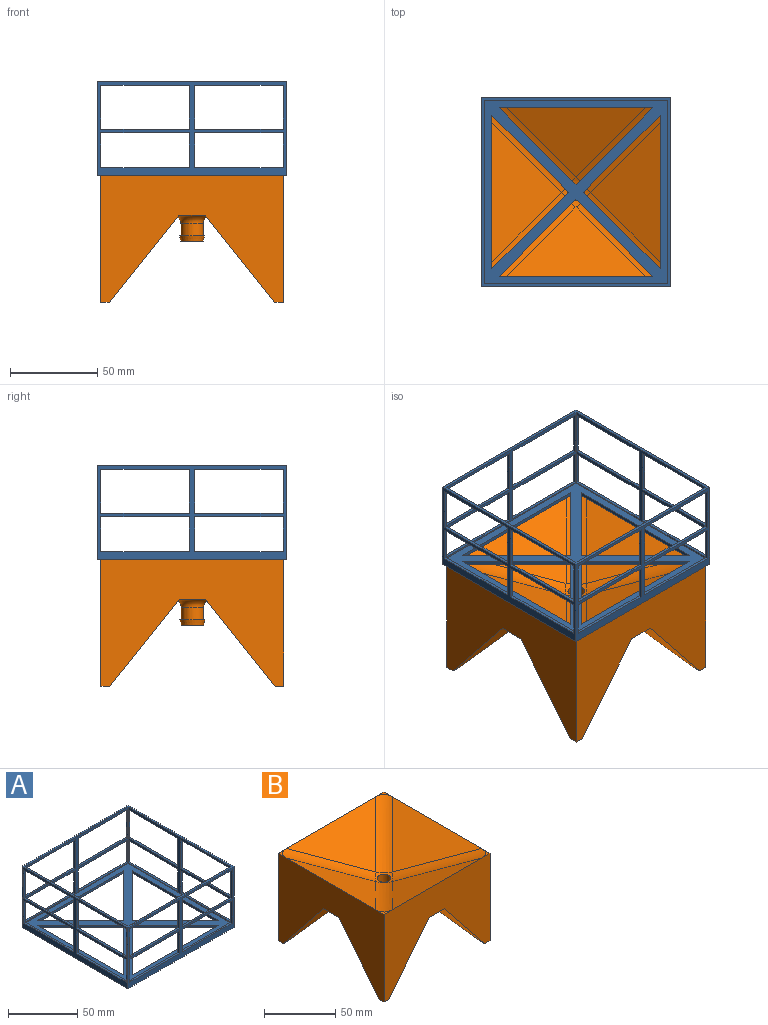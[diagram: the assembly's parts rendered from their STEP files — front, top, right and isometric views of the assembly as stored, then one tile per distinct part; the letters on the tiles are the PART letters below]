
ASSEMBLY  parts=2 mates=1
PART A: 92 faces, bbox 108.6x108.6x54 mm
  f0: plane 105.4x105.4mm, normal (0,0,1), area 3345mm2, adj f2,f3,f4,f5,f6,f7,f8,f9
  f1: plane 108.6x54mm, normal (-1,0,0), area 1272.1mm2, adj f12,f16,f19,f24,f25,f26,f27,f28
  f2: plane 105.4x50mm, normal (1,0,0), area 677.7mm2, adj f0,f19,f25,f26,f27,f28,f29,f30
  f3: plane 44.06x44.06mm, normal (0.71,0.71,0), area 124.6mm2, adj f0,f4,f17,f18
  f4: plane 44.06x44.06mm, normal (0.71,-0.71,0), area 124.6mm2, adj f0,f3,f17,f18
  f5: plane 44.06x44.06mm, normal (0.71,0.71,0), area 124.6mm2, adj f0,f6,f13,f18
  f6: plane 88.11x2mm, normal (0,-1,0), area 176.2mm2, adj f0,f5,f13,f18
  f7: plane 44.06x44.06mm, normal (0.71,-0.71,0), area 124.6mm2, adj f0,f8,f14,f18
  f8: plane 44.06x44.06mm, normal (-0.71,-0.71,0), area 124.6mm2, adj f0,f7,f14,f18
  f9: plane 88.11x2mm, normal (1,0,0), area 176.2mm2, adj f0,f10,f15,f18
  f10: plane 44.06x44.06mm, normal (-0.71,-0.71,0), area 124.6mm2, adj f0,f9,f15,f18
  f11: plane 108.6x54mm, normal (1,0,0), area 1272.1mm2, adj f12,f16,f19,f24,f59,f60,f61,f62
  f12: plane 108.6x54mm, normal (0,1,0), area 1272.1mm2, adj f1,f11,f19,f24,f76,f77,f78,f79
  f13: plane 44.06x44.06mm, normal (-0.71,0.71,0), area 124.6mm2, adj f0,f5,f6,f18
  f14: plane 88.11x2mm, normal (0,1,0), area 176.2mm2, adj f0,f7,f8,f18
  f15: plane 44.06x44.06mm, normal (-0.71,0.71,0), area 124.6mm2, adj f0,f9,f10,f18
  f16: plane 108.6x54mm, normal (0,-1,0), area 1272.1mm2, adj f1,f11,f19,f24,f42,f43,f44,f45
  f17: plane 88.11x2mm, normal (-1,0,0), area 176.2mm2, adj f0,f3,f4,f18
  f18: plane 105.4x105.4mm, normal (0,0,-1), area 3345mm2, adj f3,f4,f5,f6,f7,f8,f9,f10
  f19: plane 108.6x108.6mm, normal (0,0,1), area 684.8mm2, adj f1,f2,f11,f12,f16,f41,f58,f75
  f20: plane 105.4x2mm, normal (0,1,0), area 210.8mm2, adj f18,f21,f23,f24
  f21: plane 105.4x2mm, normal (-1,0,0), area 210.8mm2, adj f18,f20,f22,f24
  f22: plane 105.4x2mm, normal (0,-1,0), area 210.8mm2, adj f18,f21,f23,f24
  f23: plane 105.4x2mm, normal (1,0,0), area 210.8mm2, adj f18,f20,f22,f24
  f24: plane 108.6x108.6mm, normal (0,0,-1), area 684.8mm2, adj f1,f11,f12,f16,f20,f21,f22,f23
  f25: plane 50.8x1.6mm, normal (0,0,-1), area 81.3mm2, adj f1,f2,f26,f28
  f26: plane 25.2x1.6mm, normal (0,-1,0), area 40.3mm2, adj f1,f2,f25,f27
  f27: plane 50.8x1.6mm, normal (0,0,1), area 81.3mm2, adj f1,f2,f26,f28
  f28: plane 25.2x1.6mm, normal (0,1,0), area 40.3mm2, adj f1,f2,f25,f27
  f29: plane 50.8x1.6mm, normal (0,0,-1), area 81.3mm2, adj f1,f2,f30,f32
  f30: plane 20x1.6mm, normal (0,-1,0), area 32mm2, adj f1,f2,f29,f31
  f31: plane 50.8x1.6mm, normal (0,0,1), area 81.3mm2, adj f1,f2,f30,f32
  f32: plane 20x1.6mm, normal (0,1,0), area 32mm2, adj f1,f2,f29,f31
  f33: plane 50.8x1.6mm, normal (0,0,-1), area 81.3mm2, adj f1,f2,f34,f36
  f34: plane 20x1.6mm, normal (0,-1,0), area 32mm2, adj f1,f2,f33,f35
  f35: plane 50.8x1.6mm, normal (0,0,1), area 81.3mm2, adj f1,f2,f34,f36
  f36: plane 20x1.6mm, normal (0,1,0), area 32mm2, adj f1,f2,f33,f35
  f37: plane 50.8x1.6mm, normal (0,0,-1), area 81.3mm2, adj f1,f2,f38,f40
  f38: plane 25.2x1.6mm, normal (0,-1,0), area 40.3mm2, adj f1,f2,f37,f39
  f39: plane 50.8x1.6mm, normal (0,0,1), area 81.3mm2, adj f1,f2,f38,f40
  f40: plane 25.2x1.6mm, normal (0,1,0), area 40.3mm2, adj f1,f2,f37,f39
  f41: plane 105.4x50mm, normal (0,1,0), area 677.7mm2, adj f0,f2,f19,f42,f43,f44,f45,f46
  f42: plane 50.8x1.6mm, normal (0,0,-1), area 81.3mm2, adj f16,f41,f43,f45
  f43: plane 25.2x1.6mm, normal (1,0,0), area 40.3mm2, adj f16,f41,f42,f44
  f44: plane 50.8x1.6mm, normal (0,0,1), area 81.3mm2, adj f16,f41,f43,f45
  f45: plane 25.2x1.6mm, normal (-1,0,0), area 40.3mm2, adj f16,f41,f42,f44
  f46: plane 50.8x1.6mm, normal (0,0,-1), area 81.3mm2, adj f16,f41,f47,f49
  f47: plane 20x1.6mm, normal (1,0,0), area 32mm2, adj f16,f41,f46,f48
  f48: plane 50.8x1.6mm, normal (0,0,1), area 81.3mm2, adj f16,f41,f47,f49
  f49: plane 20x1.6mm, normal (-1,0,0), area 32mm2, adj f16,f41,f46,f48
  f50: plane 50.8x1.6mm, normal (0,0,-1), area 81.3mm2, adj f16,f41,f51,f53
  f51: plane 20x1.6mm, normal (1,0,0), area 32mm2, adj f16,f41,f50,f52
  f52: plane 50.8x1.6mm, normal (0,0,1), area 81.3mm2, adj f16,f41,f51,f53
  f53: plane 20x1.6mm, normal (-1,0,0), area 32mm2, adj f16,f41,f50,f52
  f54: plane 50.8x1.6mm, normal (0,0,-1), area 81.3mm2, adj f16,f41,f55,f57
  f55: plane 25.2x1.6mm, normal (1,0,0), area 40.3mm2, adj f16,f41,f54,f56
  f56: plane 50.8x1.6mm, normal (0,0,1), area 81.3mm2, adj f16,f41,f55,f57
  f57: plane 25.2x1.6mm, normal (-1,0,0), area 40.3mm2, adj f16,f41,f54,f56
  f58: plane 105.4x50mm, normal (-1,0,0), area 677.7mm2, adj f0,f19,f41,f59,f60,f61,f62,f63
  f59: plane 50.8x1.6mm, normal (0,0,-1), area 81.3mm2, adj f11,f58,f60,f62
  f60: plane 25.2x1.6mm, normal (0,1,0), area 40.3mm2, adj f11,f58,f59,f61
  f61: plane 50.8x1.6mm, normal (0,0,1), area 81.3mm2, adj f11,f58,f60,f62
  f62: plane 25.2x1.6mm, normal (0,-1,0), area 40.3mm2, adj f11,f58,f59,f61
  f63: plane 50.8x1.6mm, normal (0,0,-1), area 81.3mm2, adj f11,f58,f64,f66
  f64: plane 20x1.6mm, normal (0,1,0), area 32mm2, adj f11,f58,f63,f65
  f65: plane 50.8x1.6mm, normal (0,0,1), area 81.3mm2, adj f11,f58,f64,f66
  f66: plane 20x1.6mm, normal (0,-1,0), area 32mm2, adj f11,f58,f63,f65
  f67: plane 50.8x1.6mm, normal (0,0,-1), area 81.3mm2, adj f11,f58,f68,f70
  f68: plane 20x1.6mm, normal (0,1,0), area 32mm2, adj f11,f58,f67,f69
  f69: plane 50.8x1.6mm, normal (0,0,1), area 81.3mm2, adj f11,f58,f68,f70
  f70: plane 20x1.6mm, normal (0,-1,0), area 32mm2, adj f11,f58,f67,f69
  f71: plane 50.8x1.6mm, normal (0,0,-1), area 81.3mm2, adj f11,f58,f72,f74
  f72: plane 25.2x1.6mm, normal (0,1,0), area 40.3mm2, adj f11,f58,f71,f73
  f73: plane 50.8x1.6mm, normal (0,0,1), area 81.3mm2, adj f11,f58,f72,f74
  f74: plane 25.2x1.6mm, normal (0,-1,0), area 40.3mm2, adj f11,f58,f71,f73
  f75: plane 105.4x50mm, normal (0,-1,0), area 677.7mm2, adj f0,f2,f19,f58,f76,f77,f78,f79
  f76: plane 50.8x1.6mm, normal (0,0,-1), area 81.3mm2, adj f12,f75,f77,f79
  f77: plane 25.2x1.6mm, normal (-1,0,0), area 40.3mm2, adj f12,f75,f76,f78
  f78: plane 50.8x1.6mm, normal (0,0,1), area 81.3mm2, adj f12,f75,f77,f79
  f79: plane 25.2x1.6mm, normal (1,0,0), area 40.3mm2, adj f12,f75,f76,f78
  f80: plane 50.8x1.6mm, normal (0,0,-1), area 81.3mm2, adj f12,f75,f81,f83
  f81: plane 20x1.6mm, normal (-1,0,0), area 32mm2, adj f12,f75,f80,f82
  f82: plane 50.8x1.6mm, normal (0,0,1), area 81.3mm2, adj f12,f75,f81,f83
  f83: plane 20x1.6mm, normal (1,0,0), area 32mm2, adj f12,f75,f80,f82
  f84: plane 50.8x1.6mm, normal (0,0,-1), area 81.3mm2, adj f12,f75,f85,f87
  f85: plane 20x1.6mm, normal (-1,0,0), area 32mm2, adj f12,f75,f84,f86
  f86: plane 50.8x1.6mm, normal (0,0,1), area 81.3mm2, adj f12,f75,f85,f87
  f87: plane 20x1.6mm, normal (1,0,0), area 32mm2, adj f12,f75,f84,f86
  f88: plane 50.8x1.6mm, normal (0,0,-1), area 81.3mm2, adj f12,f75,f89,f91
  f89: plane 25.2x1.6mm, normal (-1,0,0), area 40.3mm2, adj f12,f75,f88,f90
  f90: plane 50.8x1.6mm, normal (0,0,1), area 81.3mm2, adj f12,f75,f89,f91
  f91: plane 25.2x1.6mm, normal (1,0,0), area 40.3mm2, adj f12,f75,f88,f90
PART B: 39 faces, bbox 108.7x108.7x75.8 mm
  f0: plane 43.98x15mm, normal (0,0,-1), area 630.6mm2, adj f4,f27,f34,f38
  f1: plane 43.98x15mm, normal (0,0,-1), area 630.6mm2, adj f5,f28,f36,f38
  f2: plane 43.98x15mm, normal (0,0,-1), area 630.6mm2, adj f11,f31,f37,f38
  f3: plane 43.98x15mm, normal (0,0,-1), area 630.6mm2, adj f13,f30,f33,f38
  f4: plane 105x75mm, normal (-1,0,0), area 5125mm2, adj f0,f5,f10,f13,f17,f20,f26,f27
  f5: plane 105x75mm, normal (0,-1,0), area 5125mm2, adj f1,f4,f11,f15,f17,f18,f26,f28
  f6: cylinder r=20mm len=54.34mm, axis (-0.67,0.67,0.31), area 805.6mm2, adj f10,f14,f16,f20
  f7: cylinder r=20mm len=54.34mm, axis (-0.67,-0.67,-0.31), area 805.6mm2, adj f12,f14,f16,f19
  f8: cylinder r=20mm len=54.34mm, axis (0.67,-0.67,0.31), area 805.6mm2, adj f12,f15,f16,f18
  f9: cylinder r=20mm len=54.34mm, axis (0.67,0.67,-0.31), area 805.6mm2, adj f10,f15,f16,f17
  f10: plane 88.37x44.19mm, normal (0.42,0,0.91), area 2146.6mm2, adj f4,f6,f9
  f11: plane 105x75mm, normal (1,0,0), area 5125mm2, adj f2,f5,f12,f13,f18,f19,f29,f31
  f12: plane 88.37x44.19mm, normal (-0.42,0,0.91), area 2146.6mm2, adj f7,f8,f11
  f13: plane 105x75mm, normal (0,1,0), area 5125mm2, adj f3,f4,f11,f14,f19,f20,f29,f30
  f14: plane 88.37x44.19mm, normal (0,-0.42,0.91), area 2146.6mm2, adj f6,f7,f13
  f15: plane 88.37x44.19mm, normal (0,0.42,0.91), area 2146.6mm2, adj f5,f8,f9
  f16: sphere r=20mm, area 79.7mm2, adj f6,f7,f8,f9,f21
  f17: plane 8.32x8.32mm, normal (0,0,1), area 11.9mm2, adj f4,f5,f9
  f18: plane 8.32x8.32mm, normal (0,0,1), area 11.9mm2, adj f5,f8,f11
  f19: plane 8.32x8.32mm, normal (0,0,1), area 11.9mm2, adj f7,f11,f13
  f20: plane 8.32x8.32mm, normal (0,0,1), area 11.9mm2, adj f4,f6,f13
  f21: cylinder r=4.75mm len=18.56mm, axis (0,0,-1), area 554mm2, adj f16,f25
  f22: cylinder r=6.35mm len=12.7mm, axis (0,0,1), area 279.3mm2, adj f23,f38
  f23: plane 14.29x14.29mm, normal (0,0,1), area 33.6mm2, adj f22,f24
  f24: cone r=7.14mm half-angle=14.8deg, axis (0,0,1), area 131.6mm2, adj f23,f25
  f25: plane 12.7x12.7mm, normal (0,0,-1), area 55.8mm2, adj f21,f24
  f26: plane 5x5mm, normal (0,0,-1), area 25mm2, adj f4,f5,f27,f28
  f27: plane 50x44.96mm, normal (0,0.78,-0.62), area 1600.8mm2, adj f0,f4,f26,f28,f38
  f28: plane 50x44.96mm, normal (0.78,0,-0.62), area 1600.8mm2, adj f1,f5,f26,f27,f38
  f29: plane 5x5mm, normal (0,0,-1), area 25mm2, adj f11,f13,f30,f31
  f30: plane 50x44.96mm, normal (-0.78,0,-0.62), area 1600.8mm2, adj f3,f13,f29,f31,f38
  f31: plane 50x44.96mm, normal (0,-0.78,-0.62), area 1600.8mm2, adj f2,f11,f29,f30,f38
  f32: plane 5x5mm, normal (0,0,-1), area 25mm2, adj f4,f13,f33,f34
  f33: plane 50x44.96mm, normal (0.78,0,-0.62), area 1600.8mm2, adj f3,f13,f32,f34,f38
  f34: plane 50x44.96mm, normal (0,-0.78,-0.62), area 1600.8mm2, adj f0,f4,f32,f33,f38
  f35: plane 5x5mm, normal (0,0,-1), area 25mm2, adj f5,f11,f36,f37
  f36: plane 50x44.96mm, normal (-0.78,0,-0.62), area 1600.8mm2, adj f1,f5,f35,f37,f38
  f37: plane 50x44.96mm, normal (0,0.78,-0.62), area 1600.8mm2, adj f2,f11,f35,f36,f38
  f38: torus R=11.35mm, axis (0,0,1), area 401mm2, adj f0,f1,f2,f3,f22,f27,f28,f30
PLACE A t=(28.9,56.82,26.3)mm
PLACE B t=(28.9,109.12,1.85)mm
MATE fastened B.f5 <-> A.f20  axis (0,-1,0) through (28.9,4.12,-0.7)mm
